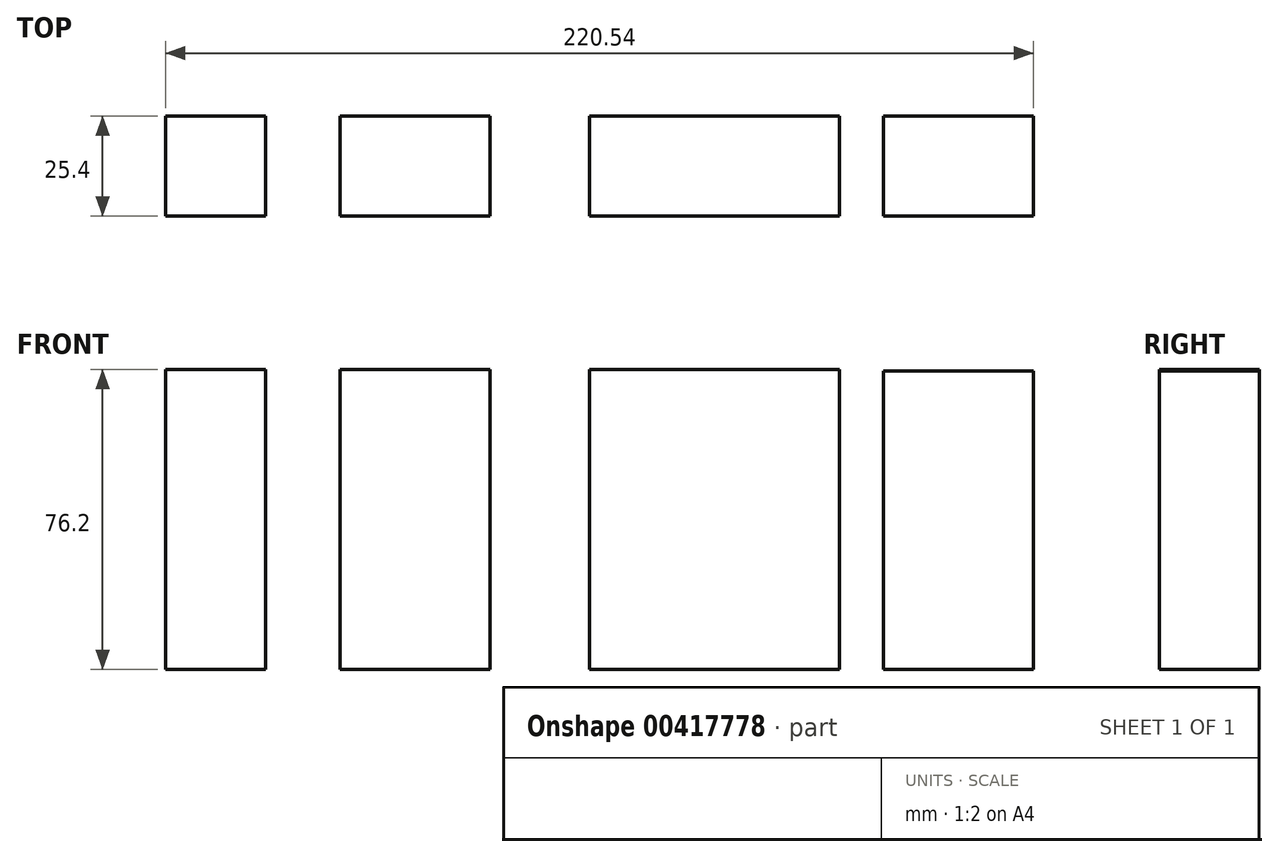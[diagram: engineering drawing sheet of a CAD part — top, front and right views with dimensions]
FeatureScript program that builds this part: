
annotation { "Feature Type Name" : "Feature", "Feature Type Description" : "" }
export const myFeature = defineFeature(function(context is Context, id is Id, definition is map)
    precondition{}
    {
        {
            var Q0;
            Q0=qCreatedBy(makeId("Front.planeOp"),FACE);
            var sketch = newSketch(context, id + "F0", { "sketchPlane" : qUnion([Q0])});
            skLineSegment(sketch, "E0.bottom", {"start": v(-112.75, -52.9) * mm, "end": v(-138.15, -52.9) * mm});
            skLineSegment(sketch, "E0.top", {"start": v(-112.75, 23.3) * mm, "end": v(-138.15, 23.3) * mm});
            skLineSegment(sketch, "E0.left", {"start": v(-112.75, -52.9) * mm, "end": v(-112.75, 23.3) * mm});
            skLineSegment(sketch, "E0.right", {"start": v(-138.15, -52.9) * mm, "end": v(-138.15, 23.3) * mm});
            skPoint(sketch, "E0.middle", {"position": v(-125.45, -14.8) * mm});
            skLineSegment(sketch, "E1.bottom", {"start": v(-93.83, 23.3) * mm, "end": v(-55.73, 23.3) * mm});
            skLineSegment(sketch, "E1.top", {"start": v(-93.83, -52.9) * mm, "end": v(-55.73, -52.9) * mm});
            skLineSegment(sketch, "E1.left", {"start": v(-93.83, 23.3) * mm, "end": v(-93.83, -52.9) * mm});
            skLineSegment(sketch, "E1.right", {"start": v(-55.73, 23.3) * mm, "end": v(-55.73, -52.9) * mm});
            skLineSegment(sketch, "E2.bottom", {"start": v(-30.45, 23.3) * mm, "end": v(33.05, 23.3) * mm});
            skLineSegment(sketch, "E2.top", {"start": v(-30.45, -52.9) * mm, "end": v(33.05, -52.9) * mm});
            skLineSegment(sketch, "E2.left", {"start": v(-30.45, 23.3) * mm, "end": v(-30.45, -52.9) * mm});
            skLineSegment(sketch, "E2.right", {"start": v(33.05, 23.3) * mm, "end": v(33.05, -52.9) * mm});
            skLineSegment(sketch, "E3.bottom", {"start": v(44.29, 22.94) * mm, "end": v(82.39, 22.94) * mm});
            skLineSegment(sketch, "E3.top", {"start": v(44.29, -52.9) * mm, "end": v(82.39, -52.9) * mm});
            skLineSegment(sketch, "E3.left", {"start": v(44.29, 22.94) * mm, "end": v(44.29, -52.9) * mm});
            skLineSegment(sketch, "E3.right", {"start": v(82.39, 22.94) * mm, "end": v(82.39, -52.9) * mm});
            skSolve(sketch);
        }
        {
            var Q0;
            Q0=makeQuery(id+"F0.imprint","IMPRINT",FACE,{"disambiguationData":[TD([[makeQuery(id+"F0.imprint","IMPRINT",EDGE,{"derivedFrom":sQuery(id+"F0.wireOp",EDGE,"E1.bottom")}),-1.0]])]});
            var Q1;
            Q1=makeQuery(id+"F0.imprint","IMPRINT",FACE,{"disambiguationData":[TD([[makeQuery(id+"F0.imprint","IMPRINT",EDGE,{"derivedFrom":sQuery(id+"F0.wireOp",EDGE,"E2.bottom")}),-1.0]])]});
            var Q2;
            Q2=makeQuery(id+"F0.imprint","IMPRINT",FACE,{"disambiguationData":[TD([[makeQuery(id+"F0.imprint","IMPRINT",EDGE,{"derivedFrom":sQuery(id+"F0.wireOp",EDGE,"E3.bottom")}),-1.0]])]});
            var Q3;
            Q3=makeQuery(id+"F0.imprint","IMPRINT",FACE,{"disambiguationData":[TD([[makeQuery(id+"F0.imprint","IMPRINT",EDGE,{"derivedFrom":sQuery(id+"F0.wireOp",EDGE,"E0.bottom")}),-1.0]])]});
            extrude(context, id + "F1", {"entities" : qUnion([Q0, Q1, Q2, Q3]), "endBound" : BoundingType.SYMMETRIC, "depth" : 25.4 * mm});
        }
    });
